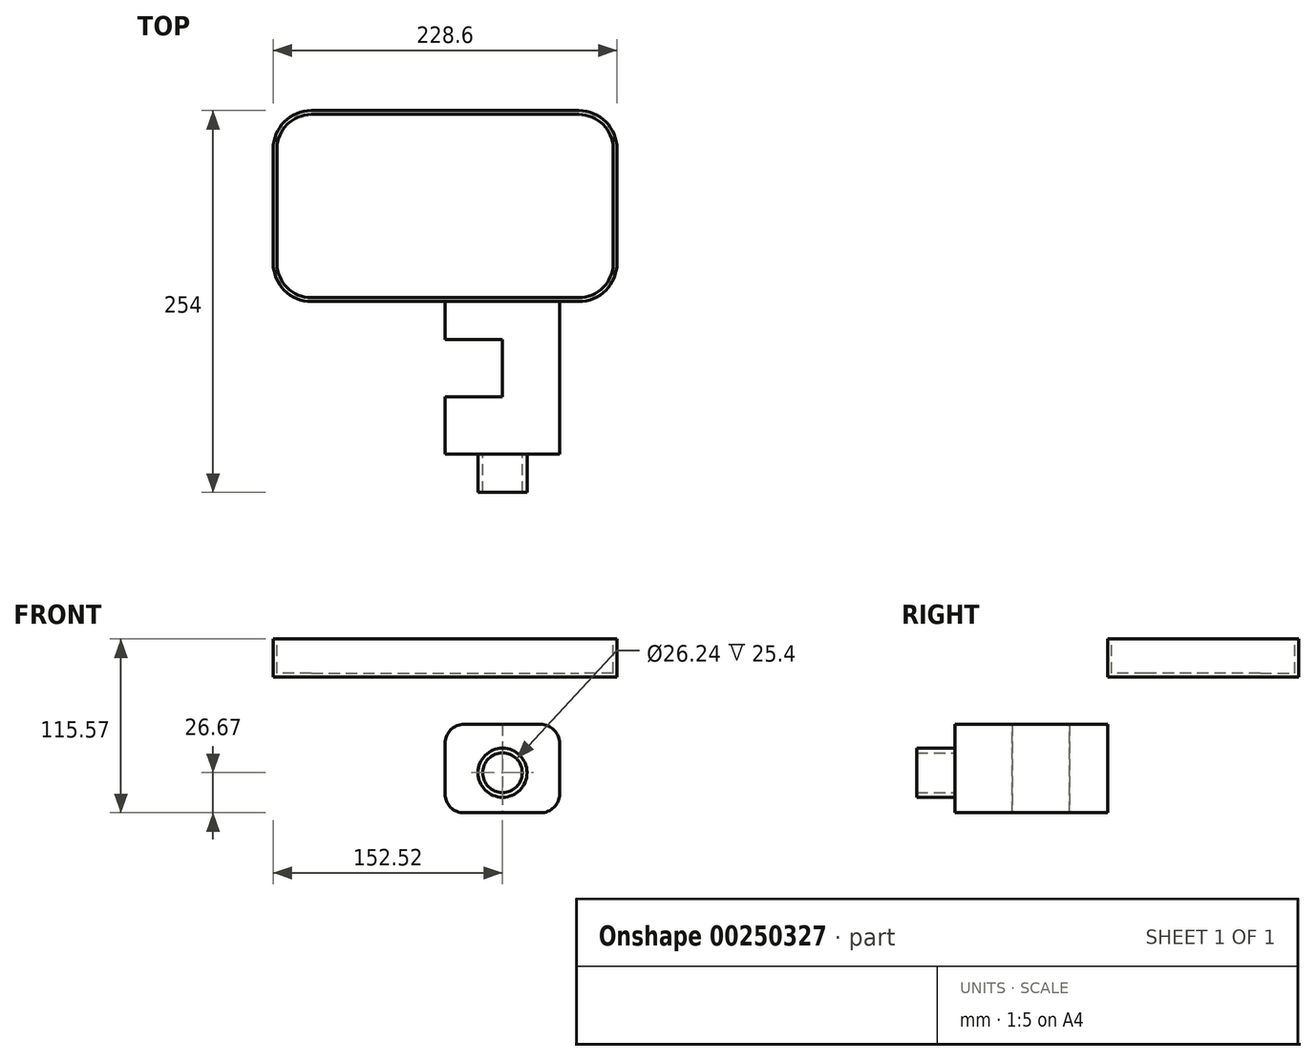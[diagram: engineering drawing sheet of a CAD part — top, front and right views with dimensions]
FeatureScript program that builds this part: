
annotation { "Feature Type Name" : "Feature", "Feature Type Description" : "" }
export const myFeature = defineFeature(function(context is Context, id is Id, definition is map)
    precondition{}
    {
        {
            var Q0;
            Q0=qCreatedBy(makeId("Front.planeOp"),FACE);
            var sketch = newSketch(context, id + "F0", { "sketchPlane" : qUnion([Q0])});
            skLineSegment(sketch, "E0.bottom", {"start": v(-88.9, -63.5) * mm, "end": v(88.9, -63.5) * mm});
            skLineSegment(sketch, "E0.top", {"start": v(-88.9, 63.5) * mm, "end": v(88.9, 63.5) * mm});
            skLineSegment(sketch, "E0.left", {"start": v(-114.3, -38.1) * mm, "end": v(-114.3, 38.1) * mm});
            skLineSegment(sketch, "E0.right", {"start": v(114.3, -38.1) * mm, "end": v(114.3, 38.1) * mm});
            skPoint(sketch, "E0.middle", {"position": v(0, 0) * mm});
            skPoint(sketch, "E1.visualSharp", {"position": v(-114.3, 63.5) * mm});
            skArc(sketch, "E1.filletArc", {"start": v(-88.9, 63.5) * mm, "mid": v(-106.86, 56.06) * mm, "end": v(-114.3, 38.1) * mm});
            skPoint(sketch, "E2.visualSharp", {"position": v(114.3, 63.5) * mm});
            skArc(sketch, "E2.filletArc", {"start": v(114.3, 38.1) * mm, "mid": v(106.86, 56.06) * mm, "end": v(88.9, 63.5) * mm});
            skPoint(sketch, "E3.visualSharp", {"position": v(114.3, -63.5) * mm});
            skArc(sketch, "E3.filletArc", {"start": v(88.9, -63.5) * mm, "mid": v(106.86, -56.06) * mm, "end": v(114.3, -38.1) * mm});
            skPoint(sketch, "E4.visualSharp", {"position": v(-114.3, -63.5) * mm});
            skArc(sketch, "E4.filletArc", {"start": v(-114.3, -38.1) * mm, "mid": v(-106.86, -56.06) * mm, "end": v(-88.9, -63.5) * mm});
            skSolve(sketch);
        }
        {
            var Q0;
            Q0 = qSketchRegion(id + "F0", true);
            extrude(context, id + "F1", {"entities" : qUnion([Q0]), "depth" : 25.4 * mm});
        }
        {
            var Q0;
            Q0=makeQuery(id+"F1.opExtrude","CAP_FACE",FACE,{"disambiguationData":[OSD([sQuery(id+"F0.wireOp",EDGE,"E0.bottom"),sQuery(id+"F0.wireOp",EDGE,"E0.top"),sQuery(id+"F0.wireOp",EDGE,"E0.left"),sQuery(id+"F0.wireOp",EDGE,"E0.right"),sQuery(id+"F0.wireOp",EDGE,"E1.filletArc"),sQuery(id+"F0.wireOp",EDGE,"E2.filletArc"),sQuery(id+"F0.wireOp",EDGE,"E3.filletArc"),sQuery(id+"F0.wireOp",EDGE,"E4.filletArc")])],"isStart":false});
            var sketch = newSketch(context, id + "F2", { "sketchPlane" : qUnion([Q0])});
            skLineSegment(sketch, "E5.bottom", {"start": v(12.63, 32.18) * mm, "end": v(63.43, 32.18) * mm});
            skLineSegment(sketch, "E5.top", {"start": v(12.63, -26.67) * mm, "end": v(63.43, -26.67) * mm});
            skLineSegment(sketch, "E5.left", {"start": v(-0.07, 19.48) * mm, "end": v(-0.07, -13.97) * mm});
            skLineSegment(sketch, "E5.right", {"start": v(76.13, 19.48) * mm, "end": v(76.13, -13.97) * mm});
            skPoint(sketch, "E6.visualSharp", {"position": v(-0.07, 32.18) * mm});
            skArc(sketch, "E6.filletArc", {"start": v(12.63, 32.18) * mm, "mid": v(3.65, 28.46) * mm, "end": v(-0.07, 19.48) * mm});
            skPoint(sketch, "E7.visualSharp", {"position": v(76.13, 32.18) * mm});
            skArc(sketch, "E7.filletArc", {"start": v(76.13, 19.48) * mm, "mid": v(72.41, 28.46) * mm, "end": v(63.43, 32.18) * mm});
            skPoint(sketch, "E8.visualSharp", {"position": v(76.13, -26.67) * mm});
            skArc(sketch, "E8.filletArc", {"start": v(63.43, -26.67) * mm, "mid": v(72.41, -22.95) * mm, "end": v(76.13, -13.97) * mm});
            skPoint(sketch, "E9.visualSharp", {"position": v(-0.07, -26.67) * mm});
            skArc(sketch, "E9.filletArc", {"start": v(-0.07, -13.97) * mm, "mid": v(3.65, -22.95) * mm, "end": v(12.63, -26.67) * mm});
            skSolve(sketch);
        }
        {
            var Q0;
            Q0=makeQuery(id+"F2.imprint","IMPRINT",FACE,{"disambiguationData":[TD([[makeQuery(id+"F2.imprint","IMPRINT",EDGE,{"derivedFrom":sQuery(id+"F2.wireOp",EDGE,"E5.bottom")}),-1.0]])]});
            extrude(context, id + "F3", {"entities" : qUnion([Q0]), "depth" : 101.6 * mm});
        }
        {
            var Q0;
            Q0=makeQuery(id+"F3.opExtrude","CAP_FACE",FACE,{"disambiguationData":[OSD([sQuery(id+"F2.wireOp",EDGE,"E5.bottom"),sQuery(id+"F2.wireOp",EDGE,"E5.top"),sQuery(id+"F2.wireOp",EDGE,"E5.left"),sQuery(id+"F2.wireOp",EDGE,"E5.right"),sQuery(id+"F2.wireOp",EDGE,"E6.filletArc"),sQuery(id+"F2.wireOp",EDGE,"E7.filletArc"),sQuery(id+"F2.wireOp",EDGE,"E8.filletArc"),sQuery(id+"F2.wireOp",EDGE,"E9.filletArc")])],"isStart":false});
            var sketch = newSketch(context, id + "F4", { "sketchPlane" : qUnion([Q0])});
            skCircle(sketch, "E10", {"center": v(38.22, 0) * mm, "radius": 16.3 * mm});
            skCircle(sketch, "E11", {"center": v(38.22, 0) * mm, "radius": 13.12 * mm});
            skSolve(sketch);
        }
        {
            var Q0;
            Q0=makeQuery(id+"F4.imprint","IMPRINT",FACE,{"disambiguationData":[TD([[makeQuery(id+"F4.imprint","IMPRINT",EDGE,{"derivedFrom":sQuery(id+"F4.wireOp",EDGE,"E10")}),1.0]])]});
            extrude(context, id + "F5", {"entities" : qUnion([Q0]), "depth" : 25.4 * mm});
        }
        {
            var Q0;
            Q0=qCreatedBy(makeId("Top.planeOp"),FACE);
            var sketch = newSketch(context, id + "F6", { "sketchPlane" : qUnion([Q0])});
            skLineSegment(sketch, "E12.bottom", {"start": v(-51.44, -50.8) * mm, "end": v(38.03, -50.8) * mm});
            skLineSegment(sketch, "E12.top", {"start": v(-51.44, -88.9) * mm, "end": v(38.03, -88.9) * mm});
            skLineSegment(sketch, "E12.left", {"start": v(-51.44, -50.8) * mm, "end": v(-51.44, -88.9) * mm});
            skLineSegment(sketch, "E12.right", {"start": v(38.03, -50.8) * mm, "end": v(38.03, -88.9) * mm});
            skSolve(sketch);
        }
        {
            var Q0;
            Q0=makeQuery(id+"F6.imprint","IMPRINT",FACE,{"disambiguationData":[TD([[makeQuery(id+"F6.imprint","IMPRINT",EDGE,{"derivedFrom":sQuery(id+"F6.wireOp",EDGE,"E12.bottom")}),-1.0]])]});
            extrude(context, id + "F7", {"entities" : qUnion([Q0]), "depth" : 76.2 * mm, "hasSecondDirection" : true, "secondDirectionOppositeDirection" : true, "secondDirectionDepth" : 76.2 * mm});
        }
        {
            var Q0;
            Q0=makeQuery(id+"F7.opExtrude","SWEPT_BODY",BODY,{"disambiguationData":[OSD([sQuery(id+"F6.wireOp",EDGE,"E12.bottom"),sQuery(id+"F6.wireOp",EDGE,"E12.top"),sQuery(id+"F6.wireOp",EDGE,"E12.left"),sQuery(id+"F6.wireOp",EDGE,"E12.right")])]});
            var Q1;
            Q1=makeQuery(id+"F3.opExtrude","SWEPT_BODY",BODY,{"disambiguationData":[OSD([sQuery(id+"F2.wireOp",EDGE,"E5.bottom"),sQuery(id+"F2.wireOp",EDGE,"E5.top"),sQuery(id+"F2.wireOp",EDGE,"E5.left"),sQuery(id+"F2.wireOp",EDGE,"E5.right"),sQuery(id+"F2.wireOp",EDGE,"E6.filletArc"),sQuery(id+"F2.wireOp",EDGE,"E7.filletArc"),sQuery(id+"F2.wireOp",EDGE,"E8.filletArc"),sQuery(id+"F2.wireOp",EDGE,"E9.filletArc")])]});
            booleanBodies(context, id + "F8", {"operationType" : BooleanOperationType.SUBTRACTION, "tools" : qUnion([Q0]), "targets" : qUnion([Q1])});
        }
        {
            var Q0;
            Q0=makeQuery(id+"F1.opExtrude","SWEPT_BODY",BODY,{"disambiguationData":[OSD([sQuery(id+"F0.wireOp",EDGE,"E0.bottom"),sQuery(id+"F0.wireOp",EDGE,"E0.top"),sQuery(id+"F0.wireOp",EDGE,"E0.left"),sQuery(id+"F0.wireOp",EDGE,"E0.right"),sQuery(id+"F0.wireOp",EDGE,"E1.filletArc"),sQuery(id+"F0.wireOp",EDGE,"E2.filletArc"),sQuery(id+"F0.wireOp",EDGE,"E3.filletArc"),sQuery(id+"F0.wireOp",EDGE,"E4.filletArc")])]});
            var Q1;
            Q1=makeQuery(id+"F1.opExtrude","CAP_EDGE",EDGE,{"disambiguationData":[OSD([sQuery(id+"F0.wireOp",EDGE,"E0.top")])],"isStart":false});
            transform(context, id + "F9", {"entities" : qUnion([Q0]), "transformType" : TransformType.ROTATION, "transformAxis" : qUnion([Q1]), "angle" : 90 * degree, "makeCopy" : false});
        }
        {
            var Q0;
            Q0=makeQuery(id+"F1.opExtrude","CAP_FACE",FACE,{"disambiguationData":[OSD([sQuery(id+"F0.wireOp",EDGE,"E0.bottom"),sQuery(id+"F0.wireOp",EDGE,"E0.top"),sQuery(id+"F0.wireOp",EDGE,"E0.left"),sQuery(id+"F0.wireOp",EDGE,"E0.right"),sQuery(id+"F0.wireOp",EDGE,"E1.filletArc"),sQuery(id+"F0.wireOp",EDGE,"E2.filletArc"),sQuery(id+"F0.wireOp",EDGE,"E3.filletArc"),sQuery(id+"F0.wireOp",EDGE,"E4.filletArc")])],"isStart":true});
            shell(context, id + "F10", {"entities" : qUnion([Q0]), "thickness" : 2.54 * mm});
        }
    });
